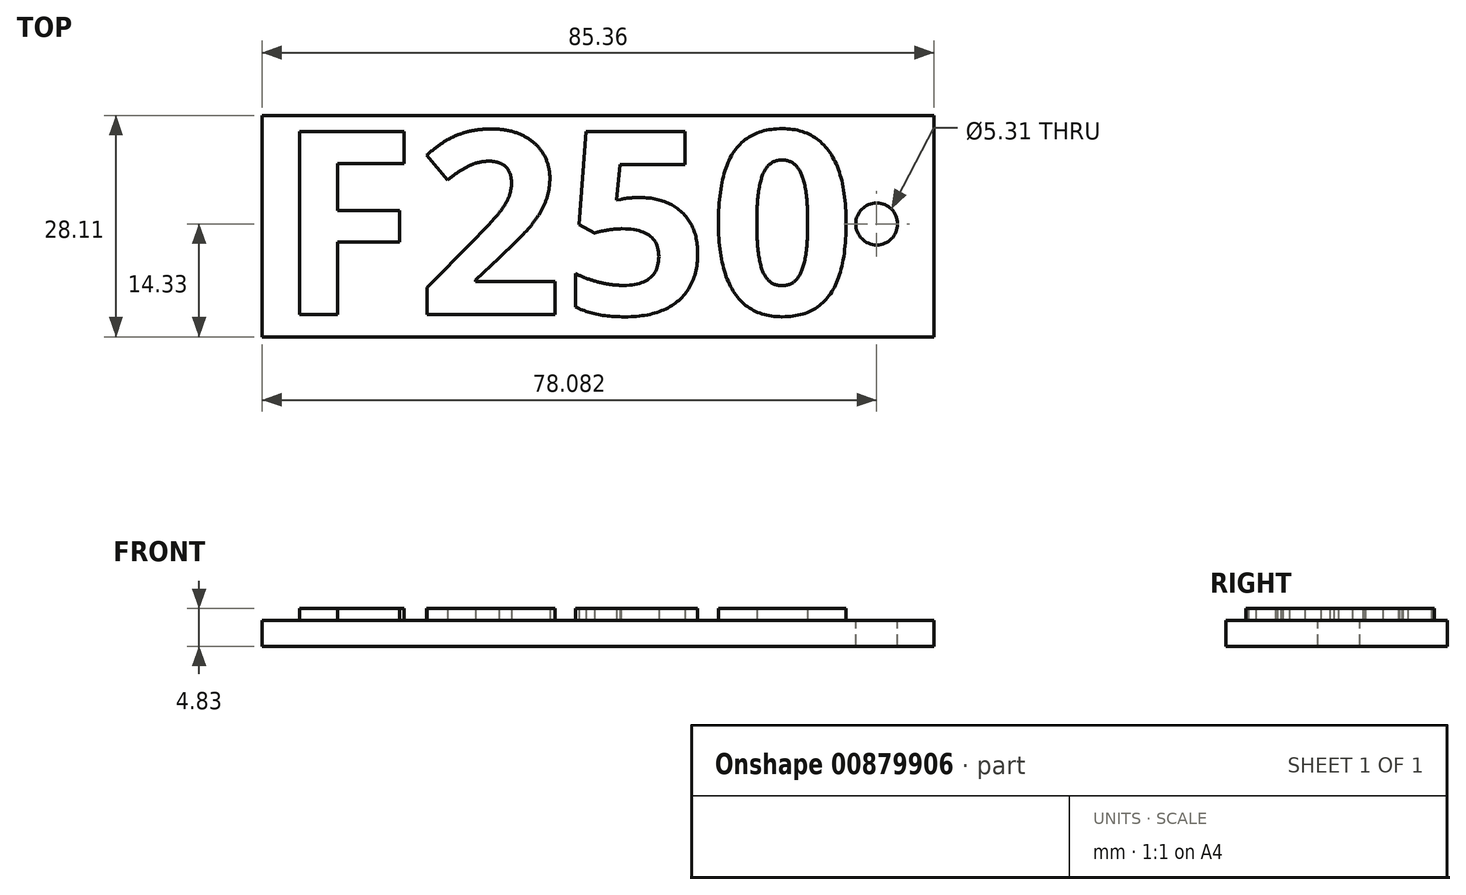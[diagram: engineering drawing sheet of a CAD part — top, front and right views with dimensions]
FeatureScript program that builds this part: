
annotation { "Feature Type Name" : "Feature", "Feature Type Description" : "" }
export const myFeature = defineFeature(function(context is Context, id is Id, definition is map)
    precondition{}
    {
        {
            var Q0;
            Q0=qCreatedBy(makeId("Top.planeOp"),FACE);
            var sketch = newSketch(context, id + "F0", { "sketchPlane" : qUnion([Q0])});
            skLineSegment(sketch, "E0.bottom", {"start": v(-50.79, 28.11) * mm, "end": v(34.57, 28.11) * mm});
            skLineSegment(sketch, "E0.top", {"start": v(-50.79, 0) * mm, "end": v(34.57, 0) * mm});
            skLineSegment(sketch, "E0.left", {"start": v(-50.79, 28.11) * mm, "end": v(-50.79, 0) * mm});
            skLineSegment(sketch, "E0.right", {"start": v(34.57, 28.11) * mm, "end": v(34.57, 0) * mm});
            skSolve(sketch);
        }
        {
            var Q0;
            Q0 = qSketchRegion(id + "F0", true);
            extrude(context, id + "F1", {"entities" : qUnion([Q0]), "depth" : 3.3 * mm, "offsetDistance" : 25.4 * mm});
        }
        {
            var Q0;
            Q0=makeQuery(id+"F1.opExtrude","CAP_FACE",FACE,{"disambiguationData":[OSD([sQuery(id+"F0.wireOp",EDGE,"E0.bottom"),sQuery(id+"F0.wireOp",EDGE,"E0.top"),sQuery(id+"F0.wireOp",EDGE,"E0.left"),sQuery(id+"F0.wireOp",EDGE,"E0.right")])],"isStart":false});
            var sketch = newSketch(context, id + "F2", { "sketchPlane" : qUnion([Q0])});
            skText(sketch, "E1", { "text": "F250", "fontName": "OpenSans-Bold.ttf"});
            const initialGuessF2  = {"E1": [-0.04895, 0.00286, 1, 0, 0.02341]};
            skSetInitialGuess(sketch, initialGuessF2);
            skSolve(sketch);
        }
        {
            var Q0;
            Q0 = qSketchRegion(id + "F2", true);
            extrude(context, id + "F3", {"entities" : qUnion([Q0]), "operationType" : NewBodyOperationType.ADD, "depth" : 1.52 * mm, "offsetDistance" : 25.4 * mm});
        }
        {
            var Q0;
            {var subQ0=sQuery(id+"F0.wireOp",EDGE,"E0.left");var subQ1=sQuery(id+"F0.wireOp",EDGE,"E0.bottom");var subQ2=sQuery(id+"F0.wireOp",EDGE,"E0.right");var subQ3=sQuery(id+"F0.wireOp",EDGE,"E0.top");Q0=makeQuery(id+"F3.boolean.opBoolean","SPLIT",FACE,{"disambiguationData":[TD([makeQuery(id+"F1.opExtrude","SWEPT_FACE",FACE,{"disambiguationData":[OSD([subQ1])]})])],"derivedFrom":makeQuery(id+"F1.opExtrude","CAP_FACE",FACE,{"disambiguationData":[OSD([subQ1,subQ3,subQ0,subQ2])],"isStart":false})});}
            var sketch = newSketch(context, id + "F4", { "sketchPlane" : qUnion([Q0])});
            skCircle(sketch, "E2", {"center": v(27.3, 14.33) * mm, "radius": 2.66 * mm});
            skSolve(sketch);
        }
        {
            var Q0;
            Q0=makeQuery(id+"F4.imprint","IMPRINT",FACE,{"disambiguationData":[TD([[makeQuery(id+"F4.imprint","IMPRINT",EDGE,{"derivedFrom":sQuery(id+"F4.wireOp",EDGE,"E2")}),1.0]])]});
            extrude(context, id + "F5", {"entities" : qUnion([Q0]), "operationType" : NewBodyOperationType.REMOVE, "oppositeDirection" : true, "depth" : 13.2 * mm, "offsetDistance" : 25.4 * mm});
        }
    });
